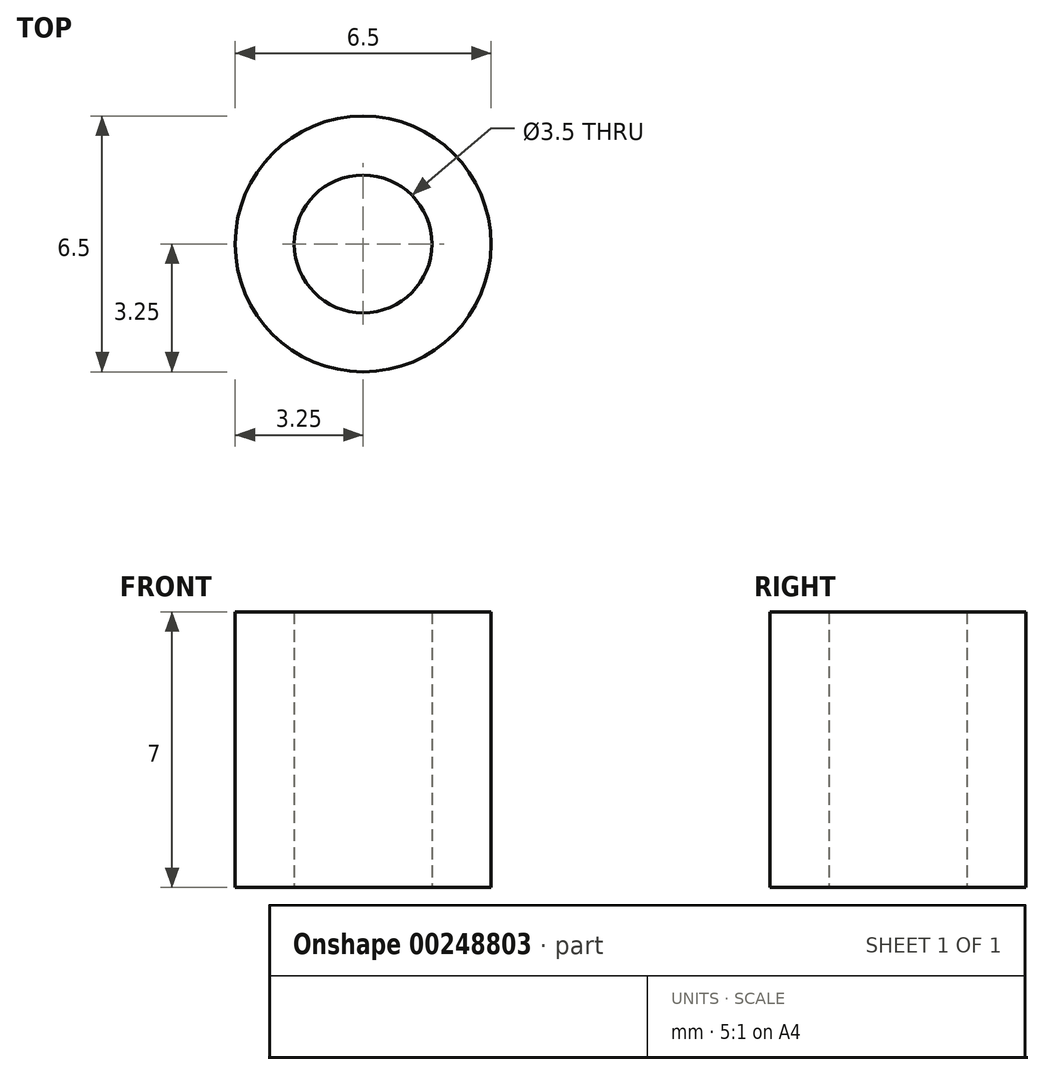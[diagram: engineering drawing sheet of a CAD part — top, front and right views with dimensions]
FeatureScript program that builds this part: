
annotation { "Feature Type Name" : "Feature", "Feature Type Description" : "" }
export const myFeature = defineFeature(function(context is Context, id is Id, definition is map)
    precondition{}
    {
        {
            var Q0;
            Q0=qCreatedBy(makeId("Top.planeOp"),FACE);
            var sketch = newSketch(context, id + "F0", { "sketchPlane" : qUnion([Q0])});
            skCircle(sketch, "E0", {"center": v(0, 0) * mm, "radius": 1.75 * mm});
            skCircle(sketch, "E1", {"center": v(0, 0) * mm, "radius": 3.25 * mm});
            skSolve(sketch);
        }
        {
            var Q0;
            Q0=makeQuery(id+"F0.imprint","IMPRINT",FACE,{"disambiguationData":[TD([[makeQuery(id+"F0.imprint","IMPRINT",EDGE,{"derivedFrom":sQuery(id+"F0.wireOp",EDGE,"E0")}),-1.0]])]});
            extrude(context, id + "F1", {"entities" : qUnion([Q0]), "depth" : 7 * mm, "offsetDistance" : 25 * mm});
        }
    });
